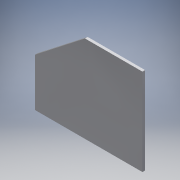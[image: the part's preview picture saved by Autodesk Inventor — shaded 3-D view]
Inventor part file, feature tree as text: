
AUTODESK INVENTOR PART (.ipt)
format: ipt  version: 2016 (Build 200138000, 138)  size: 99,840 bytes
history: native  units: in
note: dims shown in document units (in); Inventor stores cm internally (conversion verified against a paired STEP export)
features: extrude x1, sketch x1
ambient origin geometry x8: Origin, YZ Plane, XZ Plane, XY Plane, X Axis, Y Axis, Z Axis, Center Point
bodies: Body1 (feature_tree)
feature tree (2):
  extrude  "Extrusion2"  TaperAngle=90.0deg  [1 undecoded]
  sketch  "Sketch2"  dims[d4=2.2in d5=90.0deg d6=4.946in d7=4.0in d8=90.0deg d9=2.64in d10=90.0deg d11=0.125in d12=0.0in]
note: 1 required parameter value undecoded (feature->parameter linkage not recoverable at this tier; creation-order binding heuristic only, values carry confidence <= 0.55)
